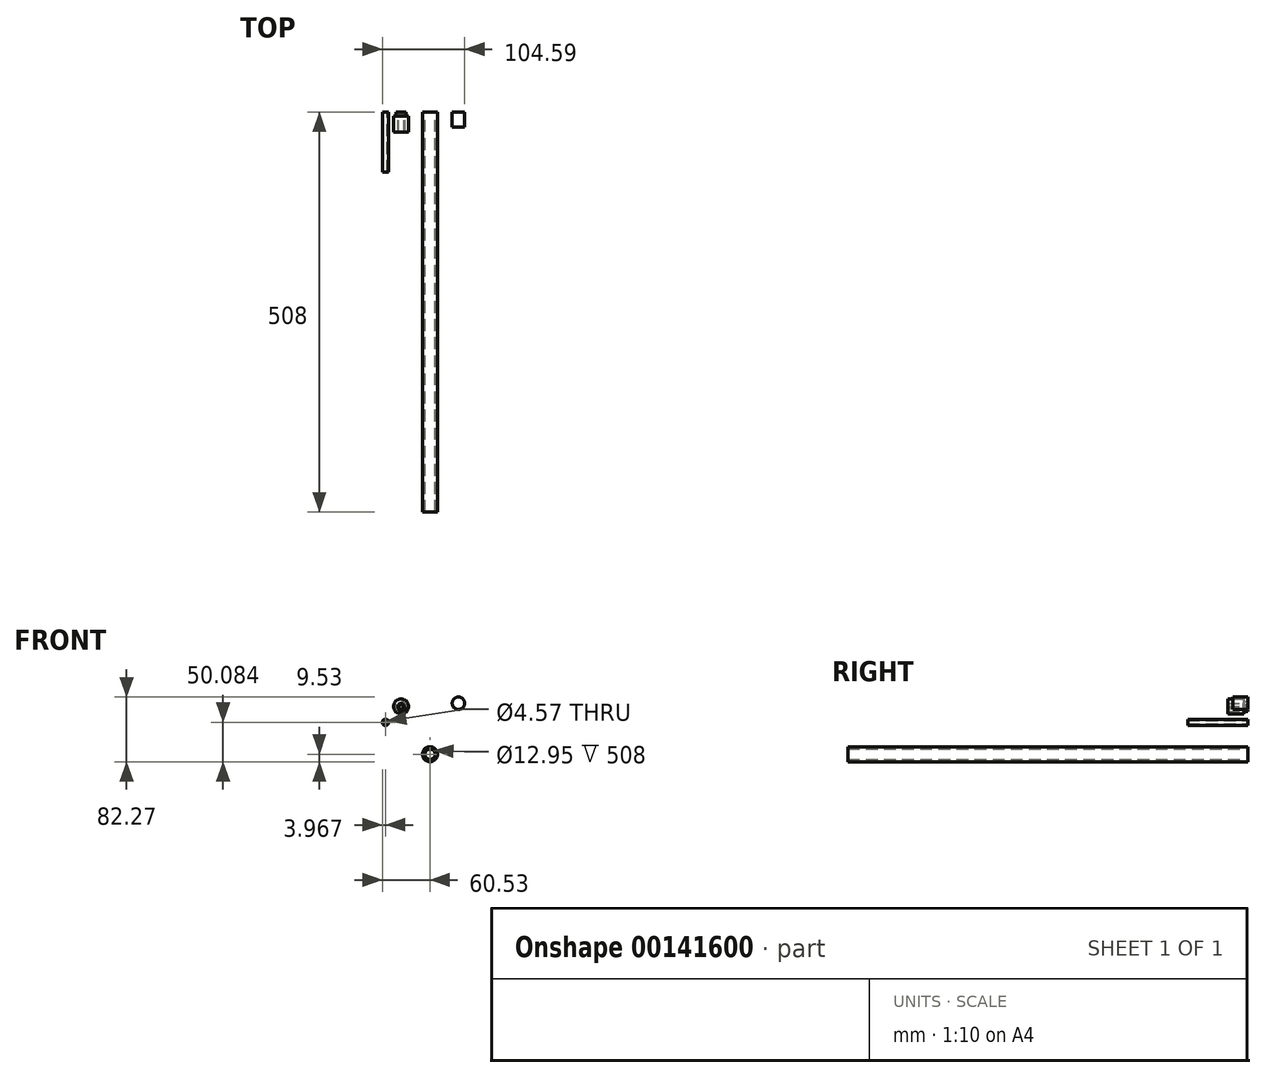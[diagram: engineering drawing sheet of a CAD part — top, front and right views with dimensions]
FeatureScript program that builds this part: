
annotation { "Feature Type Name" : "Feature", "Feature Type Description" : "" }
export const myFeature = defineFeature(function(context is Context, id is Id, definition is map)
    precondition{}
    {
        {
            var Q0;
            Q0=qCreatedBy(makeId("Front.planeOp"),FACE);
            var sketch = newSketch(context, id + "F0", { "sketchPlane" : qUnion([Q0])});
            skCircle(sketch, "E0", {"center": v(0, 0) * mm, "radius": 9.53 * mm});
            skCircle(sketch, "E1", {"center": v(0, 0) * mm, "radius": 6.48 * mm});
            skCircle(sketch, "E2", {"center": v(-36.78, 60.73) * mm, "radius": 6.48 * mm});
            skCircle(sketch, "E3", {"center": v(36.13, 64.82) * mm, "radius": 7.92 * mm});
            skCircle(sketch, "E4", {"center": v(-36.78, 60.73) * mm, "radius": 2.8 * mm});
            skCircle(sketch, "E5", {"center": v(-35.78, 58.13) * mm, "radius": 2.29 * mm});
            skCircle(sketch, "E6", {"center": v(-35.78, 58.13) * mm, "radius": 3.96 * mm});
            skCircle(sketch, "E7", {"center": v(-36.78, 60.73) * mm, "radius": 9.53 * mm});
            skCircle(sketch, "E8", {"center": v(-36.78, 60.73) * mm, "radius": 4.06 * mm});
            skCircle(sketch, "E9", {"center": v(-56.56, 40.55) * mm, "radius": 2.29 * mm});
            skCircle(sketch, "E10", {"center": v(-56.56, 40.55) * mm, "radius": 3.96 * mm});
            skSolve(sketch);
        }
        {
            var Q0;
            Q0=makeQuery(id+"F0.imprint","IMPRINT",FACE,{"disambiguationData":[TD([[makeQuery(id+"F0.imprint","IMPRINT",EDGE,{"derivedFrom":sQuery(id+"F0.wireOp",EDGE,"E0")}),1.0]])]});
            extrude(context, id + "F1", {"entities" : qUnion([Q0]), "depth" : 508 * mm});
        }
        {
            var Q0;
            Q0=makeQuery(id+"F0.imprint","IMPRINT",FACE,{"disambiguationData":[TD([[makeQuery(id+"F0.imprint","IMPRINT",EDGE,{"derivedFrom":sQuery(id+"F0.wireOp",EDGE,"E2")}),1.0]])]});
            var Q1;
            Q1=makeQuery(id+"F0.imprint","IMPRINT",FACE,{"disambiguationData":[TD([[makeQuery(id+"F0.imprint","IMPRINT",EDGE,{"derivedFrom":sQuery(id+"F0.wireOp",EDGE,"E3")}),1.0]])]});
            extrude(context, id + "F2", {"entities" : qUnion([Q0, Q1]), "depth" : 19.05 * mm});
        }
        {
            var Q0;
            Q0=makeQuery(id+"F2.opExtrude","CAP_FACE",FACE,{"disambiguationData":[OSD([sQuery(id+"F0.wireOp",EDGE,"E2"),sQuery(id+"F0.wireOp",EDGE,"E4"),sQuery(id+"F0.wireOp",EDGE,"E6")])],"isStart":false});
            extrude(context, id + "F3", {"entities" : qUnion([Q0]), "operationType" : NewBodyOperationType.ADD, "depth" : 6.35 * mm});
        }
        {
            var Q0;
            {var subQ0=sQuery(id+"F0.wireOp",EDGE,"E6");var subQ1=sQuery(id+"F0.wireOp",EDGE,"E4");var subQ2=makeQuery(id+"F0.imprint","INTERSECT",VERTEX,{"disambiguationData":[OD(0.0)],"derivedFrom":[subQ1,subQ0]});Q0=makeQuery(id+"F0.imprint","IMPRINT",FACE,{"disambiguationData":[TD([[makeQuery(id+"F0.imprint","IMPRINT",EDGE,{"disambiguationData":[TD([[subQ2,-1.0]])],"derivedFrom":subQ1}),-1.0]])]});}
            var Q1;
            {var subQ0=sQuery(id+"F0.wireOp",EDGE,"E5");var subQ1=sQuery(id+"F0.wireOp",EDGE,"E4");var subQ2=makeQuery(id+"F0.imprint","INTERSECT",VERTEX,{"disambiguationData":[OD(0.0)],"derivedFrom":[subQ1,subQ0]});Q1=makeQuery(id+"F0.imprint","IMPRINT",FACE,{"disambiguationData":[TD([[makeQuery(id+"F0.imprint","IMPRINT",EDGE,{"disambiguationData":[TD([[subQ2,-1.0]])],"derivedFrom":subQ1}),-1.0]])]});}
            var Q2;
            {var subQ0=sQuery(id+"F0.wireOp",EDGE,"E6");var subQ1=sQuery(id+"F0.wireOp",EDGE,"E4");var subQ2=makeQuery(id+"F0.imprint","INTERSECT",VERTEX,{"disambiguationData":[OD(1.0)],"derivedFrom":[subQ1,subQ0]});Q2=makeQuery(id+"F0.imprint","IMPRINT",FACE,{"disambiguationData":[TD([[makeQuery(id+"F0.imprint","IMPRINT",EDGE,{"disambiguationData":[TD([[subQ2,1.0]])],"derivedFrom":subQ1}),-1.0]])]});}
            var Q3;
            {var subQ0=sQuery(id+"F0.wireOp",EDGE,"E6");var subQ1=sQuery(id+"F0.wireOp",EDGE,"E4");var subQ2=makeQuery(id+"F0.imprint","INTERSECT",VERTEX,{"disambiguationData":[OD(0.0)],"derivedFrom":[subQ1,subQ0]});Q3=makeQuery(id+"F0.imprint","IMPRINT",FACE,{"disambiguationData":[TD([[makeQuery(id+"F0.imprint","IMPRINT",EDGE,{"disambiguationData":[TD([[subQ2,1.0]])],"derivedFrom":subQ1}),-1.0]])]});}
            extrude(context, id + "F4", {"entities" : qUnion([Q0, Q1, Q2, Q3]), "operationType" : NewBodyOperationType.ADD, "depth" : 5.6 * mm});
        }
        {
            var Q0;
            Q0=makeQuery(id+"F0.imprint","IMPRINT",FACE,{"disambiguationData":[TD([[makeQuery(id+"F0.imprint","IMPRINT",EDGE,{"derivedFrom":sQuery(id+"F0.wireOp",EDGE,"E7")}),1.0]])]});
            extrude(context, id + "F5", {"entities" : qUnion([Q0]), "operationType" : NewBodyOperationType.ADD, "depth" : 25.4 * mm, "hasSecondDirection" : true, "secondDirectionOppositeDirection" : false, "secondDirectionDepth" : 5.08 * mm});
        }
        {
            var Q0;
            {var subQ4=sQuery(id+"F0.wireOp",EDGE,"E6");var subQ5=sQuery(id+"F0.wireOp",EDGE,"E2");var subQ6=makeQuery(id+"F0.imprint","INTERSECT",VERTEX,{"disambiguationData":[OD(0.0)],"derivedFrom":[subQ5,subQ4]});Q0=makeQuery(id+"F0.imprint","IMPRINT",FACE,{"disambiguationData":[TD([[makeQuery(id+"F0.imprint","IMPRINT",EDGE,{"disambiguationData":[TD([[subQ6,-1.0]])],"derivedFrom":subQ5}),1.0]])]});}
            extrude(context, id + "F6", {"entities" : qUnion([Q0]), "operationType" : NewBodyOperationType.ADD, "depth" : 6.35 * mm});
        }
        {
            var Q0;
            {var subQ0=sQuery(id+"F0.wireOp",EDGE,"E8");var subQ1=sQuery(id+"F0.wireOp",EDGE,"E5");var subQ2=makeQuery(id+"F0.imprint","INTERSECT",VERTEX,{"disambiguationData":[OD(0.0)],"derivedFrom":[subQ1,subQ0]});Q0=makeQuery(id+"F0.imprint","IMPRINT",FACE,{"disambiguationData":[TD([[makeQuery(id+"F0.imprint","IMPRINT",EDGE,{"disambiguationData":[TD([[subQ2,1.0]])],"derivedFrom":subQ1}),1.0]])]});}
            extrude(context, id + "F7", {"entities" : qUnion([Q0]), "operationType" : NewBodyOperationType.ADD, "depth" : 5.6 * mm});
        }
        {
            var Q0;
            Q0=makeQuery(id+"F0.imprint","IMPRINT",FACE,{"disambiguationData":[TD([[makeQuery(id+"F0.imprint","IMPRINT",EDGE,{"derivedFrom":sQuery(id+"F0.wireOp",EDGE,"E9")}),-1.0]])]});
            extrude(context, id + "F8", {"entities" : qUnion([Q0]), "depth" : 76.2 * mm});
        }
    });
